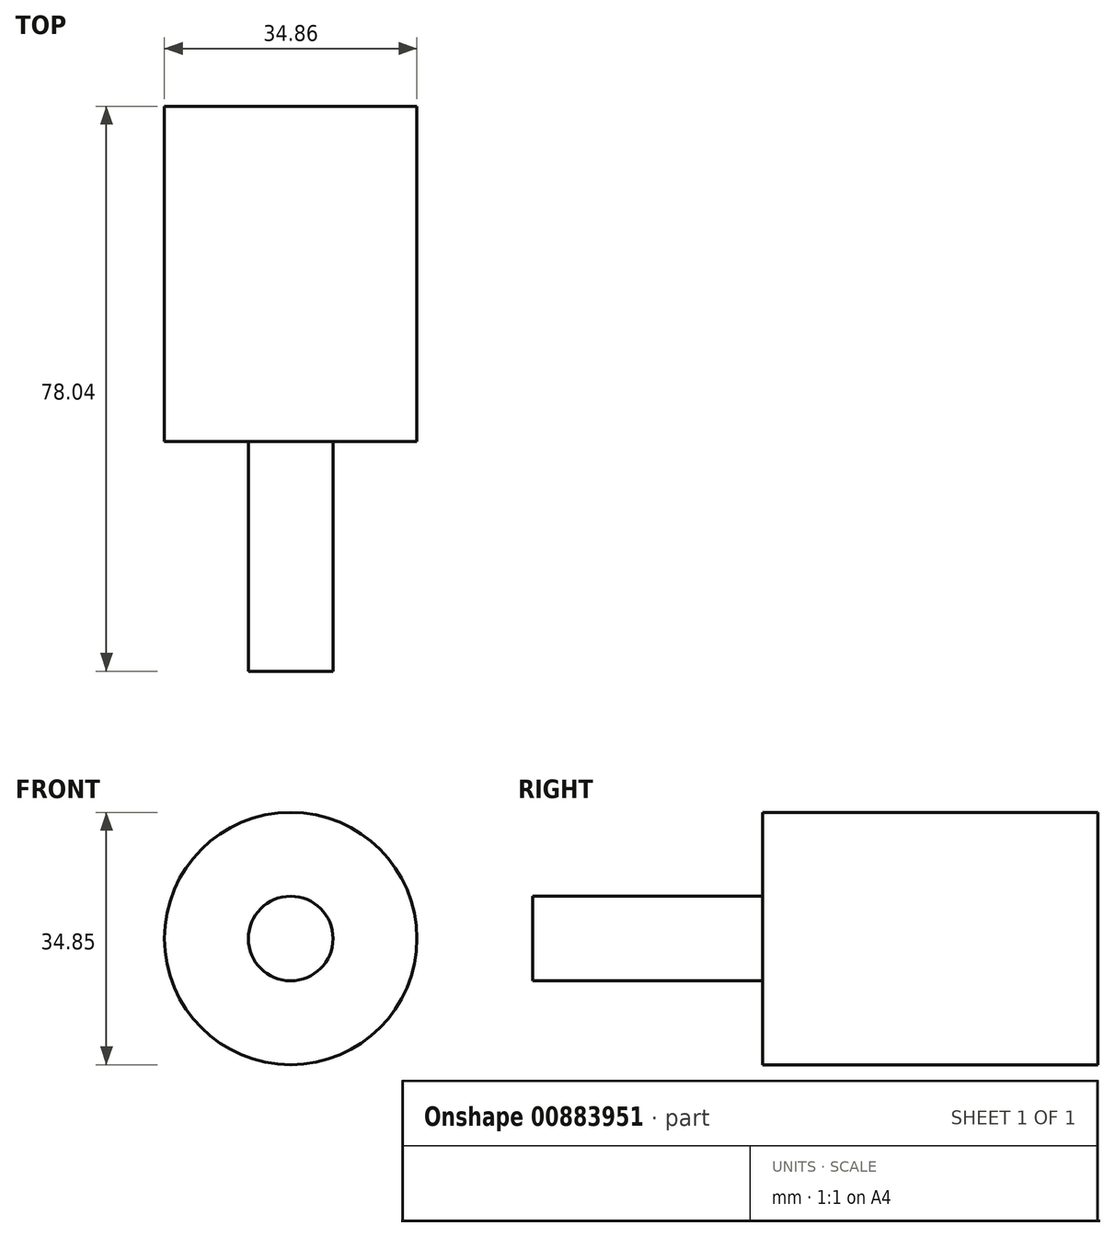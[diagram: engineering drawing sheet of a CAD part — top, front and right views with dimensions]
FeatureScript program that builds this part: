
annotation { "Feature Type Name" : "Feature", "Feature Type Description" : "" }
export const myFeature = defineFeature(function(context is Context, id is Id, definition is map)
    precondition{}
    {
        {
            var Q0;
            Q0=qCreatedBy(makeId("Right.planeOp"),FACE);
            var sketch = newSketch(context, id + "F0", { "sketchPlane" : qUnion([Q0])});
            skLineSegment(sketch, "E0.bottom", {"start": v(32.31, 12.24) * mm, "end": v(-13.98, 12.24) * mm});
            skLineSegment(sketch, "E0.top", {"start": v(32.31, 29.66) * mm, "end": v(-13.98, 29.66) * mm});
            skLineSegment(sketch, "E0.left", {"start": v(32.31, 12.24) * mm, "end": v(32.31, 29.66) * mm});
            skLineSegment(sketch, "E0.right", {"start": v(-13.98, 12.24) * mm, "end": v(-13.98, 29.66) * mm});
            skSolve(sketch);
        }
        {
            var Q0;
            Q0 = qSketchRegion(id + "F0", true);
            var Q1;
            Q1=sQuery(id+"F0.wireOp",EDGE,"E0.bottom");
            revolve(context, id + "F1", {"surfaceOperationType" : NewSurfaceOperationType.NEW, "entities" : qUnion([Q0]), "axis" : qUnion([Q1]), "revolveType" : RevolveType.FULL});
        }
        {
            var Q0;
            Q0=makeQuery(id+"F1.opRevolve","SWEPT_FACE",FACE,{"disambiguationData":[OSD([sQuery(id+"F0.wireOp",EDGE,"E0.right")])]});
            var sketch = newSketch(context, id + "F2", { "sketchPlane" : qUnion([Q0])});
            skCircle(sketch, "E1", {"center": v(0, 12.24) * mm, "radius": 5.85 * mm});
            skSolve(sketch);
        }
        {
            var Q0;
            Q0 = qSketchRegion(id + "F2", true);
            extrude(context, id + "F3", {"entities" : qUnion([Q0]), "operationType" : NewBodyOperationType.ADD, "depth" : 31.75 * mm, "offsetDistance" : 25.4 * mm});
        }
    });
